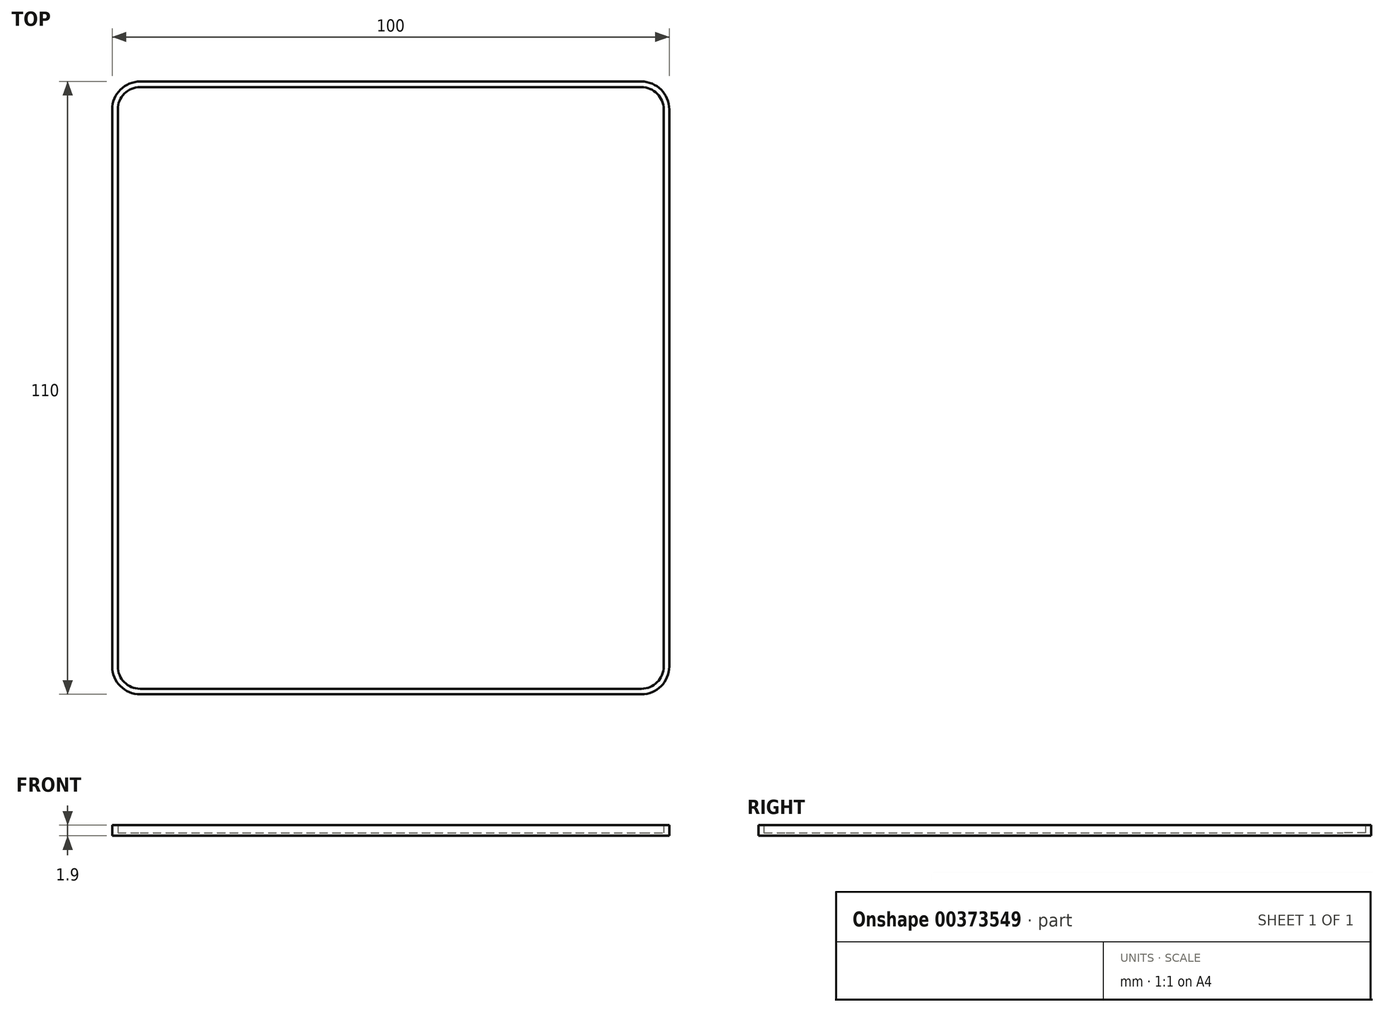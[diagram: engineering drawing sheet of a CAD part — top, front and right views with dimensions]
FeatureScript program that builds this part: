
annotation { "Feature Type Name" : "Feature", "Feature Type Description" : "" }
export const myFeature = defineFeature(function(context is Context, id is Id, definition is map)
    precondition{}
    {
        {
            var Q0;
            Q0=qCreatedBy(makeId("Top.planeOp"),FACE);
            var sketch = newSketch(context, id + "F0", { "sketchPlane" : qUnion([Q0])});
            skLineSegment(sketch, "E0.bottom", {"start": v(45, -53.92) * mm, "end": v(-45, -53.92) * mm});
            skLineSegment(sketch, "E0.top", {"start": v(45, 56.08) * mm, "end": v(-45, 56.08) * mm});
            skLineSegment(sketch, "E0.left", {"start": v(50, -48.92) * mm, "end": v(50, 51.08) * mm});
            skLineSegment(sketch, "E0.right", {"start": v(-50, -48.92) * mm, "end": v(-50, 51.08) * mm});
            skPoint(sketch, "E0.middle", {"position": v(0, 1.08) * mm});
            skPoint(sketch, "E1.visualSharp", {"position": v(-50, 56.08) * mm});
            skArc(sketch, "E1.filletArc", {"start": v(-45, 56.08) * mm, "mid": v(-48.54, 54.62) * mm, "end": v(-50, 51.08) * mm});
            skPoint(sketch, "E2.visualSharp", {"position": v(50, 56.08) * mm});
            skArc(sketch, "E2.filletArc", {"start": v(50, 51.08) * mm, "mid": v(48.54, 54.62) * mm, "end": v(45, 56.08) * mm});
            skPoint(sketch, "E3.visualSharp", {"position": v(50, -53.92) * mm});
            skArc(sketch, "E3.filletArc", {"start": v(45, -53.92) * mm, "mid": v(48.54, -52.45) * mm, "end": v(50, -48.92) * mm});
            skPoint(sketch, "E4.visualSharp", {"position": v(-50, -53.92) * mm});
            skArc(sketch, "E4.filletArc", {"start": v(-50, -48.92) * mm, "mid": v(-48.54, -52.45) * mm, "end": v(-45, -53.92) * mm});
            skSolve(sketch);
        }
        {
            var Q0;
            Q0=makeQuery(id+"F0.imprint","IMPRINT",FACE,{"disambiguationData":[TD([[makeQuery(id+"F0.imprint","IMPRINT",EDGE,{"derivedFrom":sQuery(id+"F0.wireOp",EDGE,"E0.bottom")}),-1.0]])]});
            extrude(context, id + "F1", {"entities" : qUnion([Q0]), "depth" : .5 * mm});
        }
        {
            var Q0;
            Q0=makeQuery(id+"F1.opExtrude","CAP_FACE",FACE,{"disambiguationData":[OSD([sQuery(id+"F0.wireOp",EDGE,"E0.bottom"),sQuery(id+"F0.wireOp",EDGE,"E0.top"),sQuery(id+"F0.wireOp",EDGE,"E0.left"),sQuery(id+"F0.wireOp",EDGE,"E0.right"),sQuery(id+"F0.wireOp",EDGE,"E1.filletArc"),sQuery(id+"F0.wireOp",EDGE,"E2.filletArc"),sQuery(id+"F0.wireOp",EDGE,"E3.filletArc"),sQuery(id+"F0.wireOp",EDGE,"E4.filletArc")])],"isStart":false});
            var sketch = newSketch(context, id + "F2", { "sketchPlane" : qUnion([Q0])});
            skLineSegment(sketch, "E5.0", {"start": v(49, -48.92) * mm, "end": v(49, 51.08) * mm});
            skArc(sketch, "E5.1", {"start": v(45, -52.92) * mm, "mid": v(47.83, -51.75) * mm, "end": v(49, -48.92) * mm});
            skArc(sketch, "E5.2", {"start": v(49, 51.08) * mm, "mid": v(47.83, 53.91) * mm, "end": v(45, 55.08) * mm});
            skLineSegment(sketch, "E5.3", {"start": v(-45, -52.92) * mm, "end": v(45, -52.92) * mm});
            skLineSegment(sketch, "E5.4", {"start": v(45, 55.08) * mm, "end": v(-45, 55.08) * mm});
            skArc(sketch, "E5.5", {"start": v(-45, 55.08) * mm, "mid": v(-47.83, 53.91) * mm, "end": v(-49, 51.08) * mm});
            skLineSegment(sketch, "E5.6", {"start": v(-49, 51.08) * mm, "end": v(-49, -48.92) * mm});
            skArc(sketch, "E5.7", {"start": v(-49, -48.92) * mm, "mid": v(-47.83, -51.75) * mm, "end": v(-45, -52.92) * mm});
            skLineSegment(sketch, "E6.0", {"start": v(50, -48.92) * mm, "end": v(50, 51.08) * mm});
            skArc(sketch, "E6.1", {"start": v(45, -53.92) * mm, "mid": v(48.54, -52.45) * mm, "end": v(50, -48.92) * mm});
            skArc(sketch, "E6.2", {"start": v(50, 51.08) * mm, "mid": v(48.54, 54.62) * mm, "end": v(45, 56.08) * mm});
            skLineSegment(sketch, "E6.3", {"start": v(-45, -53.92) * mm, "end": v(45, -53.92) * mm});
            skLineSegment(sketch, "E6.4", {"start": v(45, 56.08) * mm, "end": v(-45, 56.08) * mm});
            skArc(sketch, "E6.5", {"start": v(-45, 56.08) * mm, "mid": v(-48.54, 54.62) * mm, "end": v(-50, 51.08) * mm});
            skLineSegment(sketch, "E6.6", {"start": v(-50, 51.08) * mm, "end": v(-50, -48.92) * mm});
            skArc(sketch, "E6.7", {"start": v(-50, -48.92) * mm, "mid": v(-48.54, -52.45) * mm, "end": v(-45, -53.92) * mm});
            skSolve(sketch);
        }
        {
            var Q0;
            Q0 = qSketchRegion(id + "F2", true);
            extrude(context, id + "F3", {"entities" : qUnion([Q0]), "operationType" : NewBodyOperationType.ADD, "depth" : 1.4 * mm});
        }
    });
